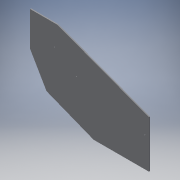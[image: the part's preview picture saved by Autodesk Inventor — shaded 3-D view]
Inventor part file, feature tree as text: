
AUTODESK INVENTOR PART (.ipt)
format: ipt  version: 2018.2 (Build 222227000, 227)  size: 135,680 bytes
history: native  units: mm
features: other x4, reference x4, extrude x3, sketch x3, chamfer x1
ambient origin geometry x8: Origin, YZ Plane, XZ Plane, XY Plane, X Axis, Y Axis, Z Axis, Center Point
bodies: Body1 (feature_tree)
feature tree (15):
  other  "ソリッド1"
  extrude  "押し出し1"  Depth=555.0mm
  extrude  "押し出し4"  Depth=560.0mm
  extrude  "押し出し5"  Depth=5.0mm TaperAngle=0.0deg
  chamfer  "面取り2"  Distance=5.0mm
  sketch  "スケッチ1"
  sketch  "スケッチ3"
  sketch  "スケッチ5"
  reference  "参照1"
  reference  "参照2"
  reference  "参照3"
  reference  "参照4"
  other  "<userpath>\Documents\Inventor\AeroCAD2018\設計\Rr.wing\model.iam"
  other  "model.iam"
  other  "endplate:1"
